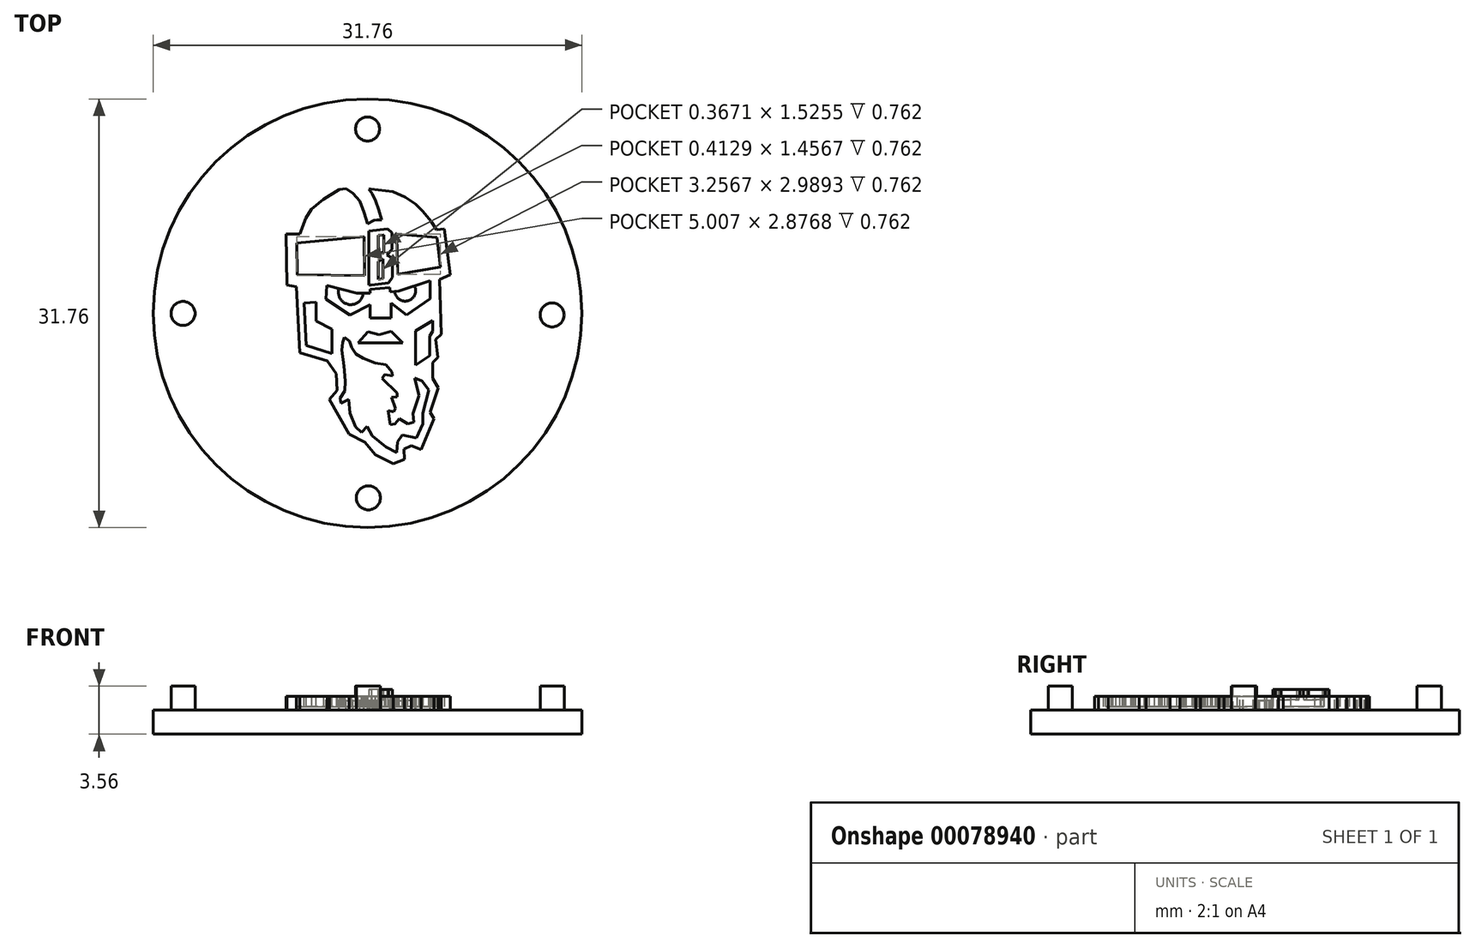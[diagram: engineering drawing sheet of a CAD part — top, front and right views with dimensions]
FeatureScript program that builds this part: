
annotation { "Feature Type Name" : "Feature", "Feature Type Description" : "" }
export const myFeature = defineFeature(function(context is Context, id is Id, definition is map)
    precondition{}
    {
        {
            var Q0;
            Q0=qCreatedBy(makeId("Top.planeOp"),FACE);
            var sketch = newSketch(context, id + "F0", { "sketchPlane" : qUnion([Q0])});
            skCircle(sketch, "E0", {"center": v(0, 0) * mm, "radius": 15.88 * mm});
            skSolve(sketch);
        }
        {
            var Q0;
            Q0=qSketchRegion(id+"F0",true);
            extrude(context, id + "F1", {"entities" : qUnion([Q0]), "oppositeDirection" : true, "depth" : 1.78 * mm});
        }
        {
            var Q0;
            Q0=makeQuery(id+"F1.opExtrude","CAP_FACE",FACE,{"disambiguationData":[OSD([sQuery(id+"F0.wireOp",EDGE,"E0")])],"isStart":true});
            var sketch = newSketch(context, id + "F2", { "sketchPlane" : qUnion([Q0])});
            skCircle(sketch, "E1", {"center": v(0, 0) * mm, "radius": 12.7 * mm});
            skSolve(sketch);
        }
        {
            var Q0;
            Q0=makeQuery(id+"F2.imprint","IMPRINT",FACE,{"disambiguationData":[TD([[makeQuery(id+"F2.imprint","IMPRINT",EDGE,{"derivedFrom":sQuery(id+"F2.wireOp",EDGE,"E1")}),-1.0]])]});
            var sketch = newSketch(context, id + "F3", { "sketchPlane" : qUnion([Q0])});
            skCircle(sketch, "E2", {"center": v(0, 13.65) * mm, "radius": 0.89 * mm});
            skCircle(sketch, "E3", {"center": v(-13.66, -0.02) * mm, "radius": 0.89 * mm});
            skCircle(sketch, "E4", {"center": v(0.06, -13.68) * mm, "radius": 0.89 * mm});
            skCircle(sketch, "E5", {"center": v(13.67, -0.12) * mm, "radius": 0.89 * mm});
            skSolve(sketch);
        }
        {
            var Q0;
            Q0=qSketchRegion(id+"F3",true);
            extrude(context, id + "F4", {"entities" : qUnion([Q0]), "operationType" : NewBodyOperationType.ADD, "depth" : 1.78 * mm});
        }
        {
            var Q0;
            Q0=makeQuery(id+"F2.imprint","IMPRINT",FACE,{"disambiguationData":[TD([[makeQuery(id+"F2.imprint","IMPRINT",EDGE,{"derivedFrom":sQuery(id+"F2.wireOp",EDGE,"E1")}),-1.0]])]});
            var sketch = newSketch(context, id + "F5", { "sketchPlane" : qUnion([Q0])});
            skLineSegment(sketch, "E6", {"start": v(-5.97, 2.09) * mm, "end": v(-6.04, 5.87) * mm});
            skLineSegment(sketch, "E7", {"start": v(-6.04, 5.87) * mm, "end": v(-5.01, 5.87) * mm});
            skLineSegment(sketch, "E8", {"start": v(-5.01, 5.87) * mm, "end": v(-4.57, 7.04) * mm});
            skLineSegment(sketch, "E9", {"start": v(-4.57, 7.04) * mm, "end": v(-4.15, 7.72) * mm});
            skLineSegment(sketch, "E10", {"start": v(-4.15, 7.72) * mm, "end": v(-3.26, 8.45) * mm});
            skLineSegment(sketch, "E11", {"start": v(-3.26, 8.45) * mm, "end": v(-2.1, 9.17) * mm});
            skLineSegment(sketch, "E12", {"start": v(-2.1, 9.17) * mm, "end": v(-1.1, 9.3) * mm});
            skLineSegment(sketch, "E13", {"start": v(-1.1, 9.3) * mm, "end": v(0.25, 9.2) * mm});
            skLineSegment(sketch, "E14", {"start": v(0.25, 9.2) * mm, "end": v(1.86, 9) * mm});
            skLineSegment(sketch, "E15", {"start": v(1.86, 9) * mm, "end": v(2.79, 8.58) * mm});
            skLineSegment(sketch, "E16", {"start": v(2.79, 8.58) * mm, "end": v(3.55, 8.1) * mm});
            skLineSegment(sketch, "E17", {"start": v(3.55, 8.1) * mm, "end": v(4.1, 7.55) * mm});
            skLineSegment(sketch, "E18", {"start": v(4.1, 7.55) * mm, "end": v(4.71, 6.83) * mm});
            skLineSegment(sketch, "E19", {"start": v(4.71, 6.83) * mm, "end": v(5.13, 6.18) * mm});
            skLineSegment(sketch, "E20", {"start": v(5.13, 6.18) * mm, "end": v(5.68, 6.25) * mm});
            skLineSegment(sketch, "E21", {"start": v(5.68, 6.25) * mm, "end": v(6.12, 2.84) * mm});
            skLineSegment(sketch, "E22", {"start": v(6.12, 2.84) * mm, "end": v(5.33, 2.5) * mm});
            skLineSegment(sketch, "E23", {"start": v(5.47, -1.56) * mm, "end": v(5.06, -1.93) * mm});
            skLineSegment(sketch, "E24", {"start": v(5.06, -1.93) * mm, "end": v(5.2, -3.27) * mm});
            skLineSegment(sketch, "E25", {"start": v(5.2, -3.27) * mm, "end": v(4.82, -3.65) * mm});
            skLineSegment(sketch, "E26", {"start": v(4.82, -3.65) * mm, "end": v(4.82, -4.82) * mm});
            skLineSegment(sketch, "E27", {"start": v(4.82, -4.82) * mm, "end": v(5.23, -5.54) * mm});
            skLineSegment(sketch, "E28", {"start": v(5.23, -5.54) * mm, "end": v(4.65, -7.33) * mm});
            skLineSegment(sketch, "E29", {"start": v(4.65, -7.33) * mm, "end": v(4.92, -7.81) * mm});
            skLineSegment(sketch, "E30", {"start": v(4.92, -7.81) * mm, "end": v(3.96, -10.11) * mm});
            skLineSegment(sketch, "E31", {"start": v(3.96, -10.11) * mm, "end": v(3.24, -9.8) * mm});
            skLineSegment(sketch, "E32", {"start": v(3.24, -9.8) * mm, "end": v(2.69, -10.08) * mm});
            skLineSegment(sketch, "E33", {"start": v(2.69, -10.08) * mm, "end": v(2.72, -10.84) * mm});
            skLineSegment(sketch, "E34", {"start": v(2.72, -10.84) * mm, "end": v(1.9, -11.15) * mm});
            skLineSegment(sketch, "E35", {"start": v(1.9, -11.15) * mm, "end": v(0.59, -10.5) * mm});
            skLineSegment(sketch, "E36", {"start": v(0.59, -10.5) * mm, "end": v(-0.2, -9.56) * mm});
            skLineSegment(sketch, "E37", {"start": v(-0.2, -9.56) * mm, "end": v(-1.37, -8.95) * mm});
            skLineSegment(sketch, "E38", {"start": v(-1.37, -8.95) * mm, "end": v(-2.81, -6.4) * mm});
            skLineSegment(sketch, "E39", {"start": v(-2.81, -6.4) * mm, "end": v(-2.26, -5.71) * mm});
            skLineSegment(sketch, "E40", {"start": v(-2.26, -5.71) * mm, "end": v(-2.33, -4.48) * mm});
            skLineSegment(sketch, "E41", {"start": v(-2.33, -4.48) * mm, "end": v(-2.98, -3.52) * mm});
            skLineSegment(sketch, "E42", {"start": v(-2.98, -3.52) * mm, "end": v(-5.01, -2.93) * mm});
            skLineSegment(sketch, "E43", {"start": v(-5.25, 1.95) * mm, "end": v(-5.97, 2.09) * mm});
            skLineSegment(sketch, "E44", {"start": v(-5.25, 1.95) * mm, "end": v(-5.01, -2.93) * mm});
            skLineSegment(sketch, "E45", {"start": v(5.33, 2.5) * mm, "end": v(5.47, -1.56) * mm});
            skSolve(sketch);
        }
        {
            var Q0;
            Q0 = qSketchRegion(id + "F5", true);
            extrude(context, id + "F6", {"entities" : qUnion([Q0]), "operationType" : NewBodyOperationType.ADD, "depth" : 1.02 * mm});
        }
        {
            var Q0;
            Q0=makeQuery(id+"F6.opExtrude","CAP_FACE",FACE,{"disambiguationData":[OSD([sQuery(id+"F5.wireOp",EDGE,"E6"),sQuery(id+"F5.wireOp",EDGE,"E7"),sQuery(id+"F5.wireOp",EDGE,"E8"),sQuery(id+"F5.wireOp",EDGE,"E9"),sQuery(id+"F5.wireOp",EDGE,"E10"),sQuery(id+"F5.wireOp",EDGE,"E11"),sQuery(id+"F5.wireOp",EDGE,"E12"),sQuery(id+"F5.wireOp",EDGE,"E13"),sQuery(id+"F5.wireOp",EDGE,"E14"),sQuery(id+"F5.wireOp",EDGE,"E15"),sQuery(id+"F5.wireOp",EDGE,"E16"),sQuery(id+"F5.wireOp",EDGE,"E17"),sQuery(id+"F5.wireOp",EDGE,"E18"),sQuery(id+"F5.wireOp",EDGE,"E19"),sQuery(id+"F5.wireOp",EDGE,"E20"),sQuery(id+"F5.wireOp",EDGE,"E21"),sQuery(id+"F5.wireOp",EDGE,"E22"),sQuery(id+"F5.wireOp",EDGE,"E23"),sQuery(id+"F5.wireOp",EDGE,"E24"),sQuery(id+"F5.wireOp",EDGE,"E25"),sQuery(id+"F5.wireOp",EDGE,"E26"),sQuery(id+"F5.wireOp",EDGE,"E27"),sQuery(id+"F5.wireOp",EDGE,"E28"),sQuery(id+"F5.wireOp",EDGE,"E29"),sQuery(id+"F5.wireOp",EDGE,"E30"),sQuery(id+"F5.wireOp",EDGE,"E31"),sQuery(id+"F5.wireOp",EDGE,"E32"),sQuery(id+"F5.wireOp",EDGE,"E33"),sQuery(id+"F5.wireOp",EDGE,"E34"),sQuery(id+"F5.wireOp",EDGE,"E35"),sQuery(id+"F5.wireOp",EDGE,"E36"),sQuery(id+"F5.wireOp",EDGE,"E37"),sQuery(id+"F5.wireOp",EDGE,"E38"),sQuery(id+"F5.wireOp",EDGE,"E39"),sQuery(id+"F5.wireOp",EDGE,"E40"),sQuery(id+"F5.wireOp",EDGE,"E41"),sQuery(id+"F5.wireOp",EDGE,"E42"),sQuery(id+"F5.wireOp",EDGE,"E43"),sQuery(id+"F5.wireOp",EDGE,"E44"),sQuery(id+"F5.wireOp",EDGE,"E45")])],"isStart":false});
            var sketch = newSketch(context, id + "F7", { "sketchPlane" : qUnion([Q0])});
            skLineSegment(sketch, "E46", {"start": v(1.76, 2.54) * mm, "end": v(1.56, 2.25) * mm});
            skLineSegment(sketch, "E47", {"start": v(1.56, 2.25) * mm, "end": v(0.29, 2.1) * mm});
            skLineSegment(sketch, "E48", {"start": v(1.5, 6.25) * mm, "end": v(0.11, 6.1) * mm});
            skLineSegment(sketch, "E49", {"start": v(0.11, 6.1) * mm, "end": v(0.11, 2.08) * mm});
            skLineSegment(sketch, "E50", {"start": v(0.11, 2.08) * mm, "end": v(0.29, 2.1) * mm});
            skLineSegment(sketch, "E51", {"start": v(1.76, 2.54) * mm, "end": v(1.85, 2.68) * mm});
            skLineSegment(sketch, "E52", {"start": v(1.85, 2.68) * mm, "end": v(1.85, 4.08) * mm});
            skLineSegment(sketch, "E53", {"start": v(1.82, 4.72) * mm, "end": v(1.82, 5.96) * mm});
            skLineSegment(sketch, "E54", {"start": v(1.82, 5.96) * mm, "end": v(1.5, 6.25) * mm});
            skLineSegment(sketch, "E55", {"start": v(1.85, 4.08) * mm, "end": v(1.44, 4.32) * mm});
            skLineSegment(sketch, "E56", {"start": v(1.44, 4.32) * mm, "end": v(1.82, 4.72) * mm});
            skSolve(sketch);
        }
        {
            var Q0;
            Q0 = qSketchRegion(id + "F7", true);
            extrude(context, id + "F8", {"entities" : qUnion([Q0]), "operationType" : NewBodyOperationType.ADD, "depth" : 0.5 * mm});
        }
        {
            var Q0;
            Q0=makeQuery(id+"F8.opExtrude","CAP_FACE",FACE,{"disambiguationData":[OSD([sQuery(id+"F7.wireOp",EDGE,"fYX4uZuE-G3KO-kAFN-Q3tX-kjtKbBJFoakh"),sQuery(id+"F7.wireOp",EDGE,"YPmriUSY-hdAp-dQCe-8mBx-pWrRA5I0jtpz"),sQuery(id+"F7.wireOp",EDGE,"z7Qzhmuc-i2NW-aavj-4vSp-u2Y9M5CnwlP8"),sQuery(id+"F7.wireOp",EDGE,"ckSUy8qp-SA3c-FUe3-0Q31-KxK1UnF4vGYb"),sQuery(id+"F7.wireOp",EDGE,"sxyVmpqT-fyA1-mW33-j374-GcPe8uCOevbE"),sQuery(id+"F7.wireOp",EDGE,"K1yYejpL-Rl0o-4VMU-6FDC-4IuAW9tG96Hq"),sQuery(id+"F7.wireOp",EDGE,"E46"),sQuery(id+"F7.wireOp",EDGE,"E47"),sQuery(id+"F7.wireOp",EDGE,"CEOLPyhg-Qa5c-qZ7R-2YQ4-FfNo4KrpU84Y")])],"isStart":false});
            var sketch = newSketch(context, id + "F9", { "sketchPlane" : qUnion([Q0])});
            skLineSegment(sketch, "E57", {"start": v(0.78, 4.36) * mm, "end": v(1.2, 4.58) * mm});
            skLineSegment(sketch, "E58", {"start": v(1.2, 4.58) * mm, "end": v(1.2, 5.82) * mm});
            skLineSegment(sketch, "E59", {"start": v(1.2, 5.82) * mm, "end": v(0.8, 5.76) * mm});
            skLineSegment(sketch, "E60", {"start": v(0.8, 5.76) * mm, "end": v(0.78, 4.36) * mm});
            skLineSegment(sketch, "E61", {"start": v(0.8, 3.84) * mm, "end": v(0.8, 2.5) * mm});
            skLineSegment(sketch, "E62", {"start": v(0.8, 2.5) * mm, "end": v(1.16, 2.57) * mm});
            skLineSegment(sketch, "E63", {"start": v(1.16, 2.57) * mm, "end": v(1.16, 4.03) * mm});
            skLineSegment(sketch, "E64", {"start": v(1.16, 4.03) * mm, "end": v(0.8, 3.84) * mm});
            skSolve(sketch);
        }
        {
            var Q0;
            Q0 = qSketchRegion(id + "F9", true);
            extrude(context, id + "F10", {"entities" : qUnion([Q0]), "operationType" : NewBodyOperationType.REMOVE, "oppositeDirection" : true, "depth" : 0.76 * mm});
        }
        {
            var Q0;
            Q0=makeQuery(id+"F6.opExtrude","CAP_FACE",FACE,{"disambiguationData":[OSD([sQuery(id+"F5.wireOp",EDGE,"E6"),sQuery(id+"F5.wireOp",EDGE,"E7"),sQuery(id+"F5.wireOp",EDGE,"E8"),sQuery(id+"F5.wireOp",EDGE,"E9"),sQuery(id+"F5.wireOp",EDGE,"E10"),sQuery(id+"F5.wireOp",EDGE,"E11"),sQuery(id+"F5.wireOp",EDGE,"E12"),sQuery(id+"F5.wireOp",EDGE,"E13"),sQuery(id+"F5.wireOp",EDGE,"E14"),sQuery(id+"F5.wireOp",EDGE,"E15"),sQuery(id+"F5.wireOp",EDGE,"E16"),sQuery(id+"F5.wireOp",EDGE,"E17"),sQuery(id+"F5.wireOp",EDGE,"E18"),sQuery(id+"F5.wireOp",EDGE,"E19"),sQuery(id+"F5.wireOp",EDGE,"E20"),sQuery(id+"F5.wireOp",EDGE,"E21"),sQuery(id+"F5.wireOp",EDGE,"E22"),sQuery(id+"F5.wireOp",EDGE,"E23"),sQuery(id+"F5.wireOp",EDGE,"E24"),sQuery(id+"F5.wireOp",EDGE,"E25"),sQuery(id+"F5.wireOp",EDGE,"E26"),sQuery(id+"F5.wireOp",EDGE,"E27"),sQuery(id+"F5.wireOp",EDGE,"E28"),sQuery(id+"F5.wireOp",EDGE,"E29"),sQuery(id+"F5.wireOp",EDGE,"E30"),sQuery(id+"F5.wireOp",EDGE,"E31"),sQuery(id+"F5.wireOp",EDGE,"E32"),sQuery(id+"F5.wireOp",EDGE,"E33"),sQuery(id+"F5.wireOp",EDGE,"E34"),sQuery(id+"F5.wireOp",EDGE,"E35"),sQuery(id+"F5.wireOp",EDGE,"E36"),sQuery(id+"F5.wireOp",EDGE,"E37"),sQuery(id+"F5.wireOp",EDGE,"E38"),sQuery(id+"F5.wireOp",EDGE,"E39"),sQuery(id+"F5.wireOp",EDGE,"E40"),sQuery(id+"F5.wireOp",EDGE,"E41"),sQuery(id+"F5.wireOp",EDGE,"E42"),sQuery(id+"F5.wireOp",EDGE,"E43"),sQuery(id+"F5.wireOp",EDGE,"E44"),sQuery(id+"F5.wireOp",EDGE,"E45")])],"isStart":false});
            var sketch = newSketch(context, id + "F11", { "sketchPlane" : qUnion([Q0])});
            skLineSegment(sketch, "E65", {"start": v(-5.23, 5.2) * mm, "end": v(-5.2, 2.85) * mm});
            skLineSegment(sketch, "E66", {"start": v(-5.2, 2.85) * mm, "end": v(-0.22, 2.8) * mm});
            skLineSegment(sketch, "E67", {"start": v(-0.22, 2.8) * mm, "end": v(-0.24, 5.68) * mm});
            skLineSegment(sketch, "E68", {"start": v(-0.24, 5.68) * mm, "end": v(-5.23, 5.2) * mm});
            skLineSegment(sketch, "E69", {"start": v(2.15, 5.87) * mm, "end": v(5.14, 5.6) * mm});
            skLineSegment(sketch, "E70", {"start": v(5.14, 5.6) * mm, "end": v(5.41, 3.42) * mm});
            skLineSegment(sketch, "E71", {"start": v(5.41, 3.42) * mm, "end": v(2.23, 2.88) * mm});
            skLineSegment(sketch, "E72", {"start": v(2.23, 2.88) * mm, "end": v(2.15, 5.87) * mm});
            skSolve(sketch);
        }
        {
            var Q0;
            Q0 = qSketchRegion(id + "F11", true);
            extrude(context, id + "F12", {"entities" : qUnion([Q0]), "operationType" : NewBodyOperationType.REMOVE, "oppositeDirection" : true, "depth" : 0.76 * mm});
        }
        {
            var Q0;
            Q0=makeQuery(id+"F6.opExtrude","CAP_FACE",FACE,{"disambiguationData":[OSD([sQuery(id+"F5.wireOp",EDGE,"E6"),sQuery(id+"F5.wireOp",EDGE,"E7"),sQuery(id+"F5.wireOp",EDGE,"E8"),sQuery(id+"F5.wireOp",EDGE,"E9"),sQuery(id+"F5.wireOp",EDGE,"E10"),sQuery(id+"F5.wireOp",EDGE,"E11"),sQuery(id+"F5.wireOp",EDGE,"E12"),sQuery(id+"F5.wireOp",EDGE,"E13"),sQuery(id+"F5.wireOp",EDGE,"E14"),sQuery(id+"F5.wireOp",EDGE,"E15"),sQuery(id+"F5.wireOp",EDGE,"E16"),sQuery(id+"F5.wireOp",EDGE,"E17"),sQuery(id+"F5.wireOp",EDGE,"E18"),sQuery(id+"F5.wireOp",EDGE,"E19"),sQuery(id+"F5.wireOp",EDGE,"E20"),sQuery(id+"F5.wireOp",EDGE,"E21"),sQuery(id+"F5.wireOp",EDGE,"E22"),sQuery(id+"F5.wireOp",EDGE,"E23"),sQuery(id+"F5.wireOp",EDGE,"E24"),sQuery(id+"F5.wireOp",EDGE,"E25"),sQuery(id+"F5.wireOp",EDGE,"E26"),sQuery(id+"F5.wireOp",EDGE,"E27"),sQuery(id+"F5.wireOp",EDGE,"E28"),sQuery(id+"F5.wireOp",EDGE,"E29"),sQuery(id+"F5.wireOp",EDGE,"E30"),sQuery(id+"F5.wireOp",EDGE,"E31"),sQuery(id+"F5.wireOp",EDGE,"E32"),sQuery(id+"F5.wireOp",EDGE,"E33"),sQuery(id+"F5.wireOp",EDGE,"E34"),sQuery(id+"F5.wireOp",EDGE,"E35"),sQuery(id+"F5.wireOp",EDGE,"E36"),sQuery(id+"F5.wireOp",EDGE,"E37"),sQuery(id+"F5.wireOp",EDGE,"E38"),sQuery(id+"F5.wireOp",EDGE,"E39"),sQuery(id+"F5.wireOp",EDGE,"E40"),sQuery(id+"F5.wireOp",EDGE,"E41"),sQuery(id+"F5.wireOp",EDGE,"E42"),sQuery(id+"F5.wireOp",EDGE,"E43"),sQuery(id+"F5.wireOp",EDGE,"E44"),sQuery(id+"F5.wireOp",EDGE,"E45")])],"isStart":false});
            var sketch = newSketch(context, id + "F13", { "sketchPlane" : qUnion([Q0])});
            skLineSegment(sketch, "E73", {"start": v(-3.03, 2.07) * mm, "end": v(-0.78, 1.48) * mm});
            skLineSegment(sketch, "E74", {"start": v(-0.78, 1.48) * mm, "end": v(0.2, 1.48) * mm});
            skLineSegment(sketch, "E75", {"start": v(0.2, 1.48) * mm, "end": v(0.2, 1.78) * mm});
            skLineSegment(sketch, "E76", {"start": v(0.2, 1.78) * mm, "end": v(1.65, 1.9) * mm});
            skLineSegment(sketch, "E77", {"start": v(1.65, 1.9) * mm, "end": v(1.68, 1.58) * mm});
            skLineSegment(sketch, "E78", {"start": v(1.68, 1.58) * mm, "end": v(2.32, 1.63) * mm});
            skLineSegment(sketch, "E79", {"start": v(2.32, 1.63) * mm, "end": v(4.64, 2.4) * mm});
            skLineSegment(sketch, "E80", {"start": v(4.64, 2.4) * mm, "end": v(4.64, 1.09) * mm});
            skLineSegment(sketch, "E81", {"start": v(4.64, 1.09) * mm, "end": v(2.89, -0.13) * mm});
            skLineSegment(sketch, "E82", {"start": v(2.89, -0.13) * mm, "end": v(1.73, 0.74) * mm});
            skLineSegment(sketch, "E83", {"start": v(1.73, 0.74) * mm, "end": v(1.73, -0.36) * mm});
            skLineSegment(sketch, "E84", {"start": v(1.73, -0.36) * mm, "end": v(0.18, -0.36) * mm});
            skLineSegment(sketch, "E85", {"start": v(0.18, -0.36) * mm, "end": v(0.18, 0.62) * mm});
            skLineSegment(sketch, "E86", {"start": v(0.18, 0.62) * mm, "end": v(-1.3, -0.14) * mm});
            skLineSegment(sketch, "E87", {"start": v(-1.3, -0.14) * mm, "end": v(-3.08, 1.04) * mm});
            skLineSegment(sketch, "E88", {"start": v(-3.08, 1.04) * mm, "end": v(-3.03, 2.07) * mm});
            skSolve(sketch);
        }
        {
            var Q0;
            Q0 = qSketchRegion(id + "F13", true);
            extrude(context, id + "F14", {"entities" : qUnion([Q0]), "operationType" : NewBodyOperationType.REMOVE, "oppositeDirection" : true, "depth" : 1.02 * mm});
        }
        {
            var Q0;
            Q0=makeQuery(id+"F2.imprint","IMPRINT",FACE,{"disambiguationData":[TD([[makeQuery(id+"F2.imprint","IMPRINT",EDGE,{"derivedFrom":sQuery(id+"F2.wireOp",EDGE,"E1")}),1.0]])]});
            var sketch = newSketch(context, id + "F15", { "sketchPlane" : qUnion([Q0])});
            skLineSegment(sketch, "E89", {"start": v(-2.11, 1.83) * mm, "end": v(-0.78, 1.48) * mm});
            skLineSegment(sketch, "E90", {"start": v(-0.78, 1.48) * mm, "end": v(-0.32, 1.48) * mm});
            skArc(sketch, "E91", {"start": v(-2.11, 1.83) * mm, "mid": v(-1.41, 0.65) * mm, "end": v(-0.32, 1.48) * mm});
            skLineSegment(sketch, "E92", {"start": v(3.48, 2.02) * mm, "end": v(2.32, 1.63) * mm});
            skLineSegment(sketch, "E93", {"start": v(2.32, 1.63) * mm, "end": v(2.02, 1.6) * mm});
            skArc(sketch, "E94", {"start": v(2.02, 1.6) * mm, "mid": v(3, 0.92) * mm, "end": v(3.48, 2.02) * mm});
            skSolve(sketch);
        }
        {
            var Q0;
            Q0 = qSketchRegion(id + "F15", true);
            extrude(context, id + "F16", {"entities" : qUnion([Q0]), "operationType" : NewBodyOperationType.ADD, "depth" : 0.71 * mm});
        }
        {
            var Q0;
            Q0=makeQuery(id+"F6.opExtrude","CAP_FACE",FACE,{"disambiguationData":[OSD([sQuery(id+"F5.wireOp",EDGE,"E6"),sQuery(id+"F5.wireOp",EDGE,"E7"),sQuery(id+"F5.wireOp",EDGE,"E8"),sQuery(id+"F5.wireOp",EDGE,"E9"),sQuery(id+"F5.wireOp",EDGE,"E10"),sQuery(id+"F5.wireOp",EDGE,"E11"),sQuery(id+"F5.wireOp",EDGE,"E12"),sQuery(id+"F5.wireOp",EDGE,"E13"),sQuery(id+"F5.wireOp",EDGE,"E14"),sQuery(id+"F5.wireOp",EDGE,"E15"),sQuery(id+"F5.wireOp",EDGE,"E16"),sQuery(id+"F5.wireOp",EDGE,"E17"),sQuery(id+"F5.wireOp",EDGE,"E18"),sQuery(id+"F5.wireOp",EDGE,"E19"),sQuery(id+"F5.wireOp",EDGE,"E20"),sQuery(id+"F5.wireOp",EDGE,"E21"),sQuery(id+"F5.wireOp",EDGE,"E22"),sQuery(id+"F5.wireOp",EDGE,"E23"),sQuery(id+"F5.wireOp",EDGE,"E24"),sQuery(id+"F5.wireOp",EDGE,"E25"),sQuery(id+"F5.wireOp",EDGE,"E26"),sQuery(id+"F5.wireOp",EDGE,"E27"),sQuery(id+"F5.wireOp",EDGE,"E28"),sQuery(id+"F5.wireOp",EDGE,"E29"),sQuery(id+"F5.wireOp",EDGE,"E30"),sQuery(id+"F5.wireOp",EDGE,"E31"),sQuery(id+"F5.wireOp",EDGE,"E32"),sQuery(id+"F5.wireOp",EDGE,"E33"),sQuery(id+"F5.wireOp",EDGE,"E34"),sQuery(id+"F5.wireOp",EDGE,"E35"),sQuery(id+"F5.wireOp",EDGE,"E36"),sQuery(id+"F5.wireOp",EDGE,"E37"),sQuery(id+"F5.wireOp",EDGE,"E38"),sQuery(id+"F5.wireOp",EDGE,"E39"),sQuery(id+"F5.wireOp",EDGE,"E40"),sQuery(id+"F5.wireOp",EDGE,"E41"),sQuery(id+"F5.wireOp",EDGE,"E42"),sQuery(id+"F5.wireOp",EDGE,"E43"),sQuery(id+"F5.wireOp",EDGE,"E44"),sQuery(id+"F5.wireOp",EDGE,"E45")])],"isStart":false});
            var sketch = newSketch(context, id + "F17", { "sketchPlane" : qUnion([Q0])});
            skLineSegment(sketch, "E95", {"start": v(-4.69, 0.77) * mm, "end": v(-4.53, -2.4) * mm});
            skLineSegment(sketch, "E96", {"start": v(-4.53, -2.4) * mm, "end": v(-2.62, -2.97) * mm});
            skLineSegment(sketch, "E97", {"start": v(-2.62, -2.97) * mm, "end": v(-2.62, -1.18) * mm});
            skLineSegment(sketch, "E98", {"start": v(-2.62, -1.18) * mm, "end": v(-3.81, -0.57) * mm});
            skLineSegment(sketch, "E99", {"start": v(-3.81, -0.57) * mm, "end": v(-3.81, 0.82) * mm});
            skLineSegment(sketch, "E100", {"start": v(-3.81, 0.82) * mm, "end": v(-4.69, 0.77) * mm});
            skLineSegment(sketch, "E101", {"start": v(4.84, -0.54) * mm, "end": v(4.84, -1.35) * mm});
            skLineSegment(sketch, "E102", {"start": v(4.84, -1.35) * mm, "end": v(4.6, -1.69) * mm});
            skLineSegment(sketch, "E103", {"start": v(4.6, -1.69) * mm, "end": v(4.6, -3.14) * mm});
            skLineSegment(sketch, "E104", {"start": v(4.6, -3.14) * mm, "end": v(3.57, -3.86) * mm});
            skLineSegment(sketch, "E105", {"start": v(3.57, -3.86) * mm, "end": v(3.57, -1.32) * mm});
            skLineSegment(sketch, "E106", {"start": v(3.57, -1.32) * mm, "end": v(4.84, -0.54) * mm});
            skSolve(sketch);
        }
        {
            var Q0;
            Q0 = qSketchRegion(id + "F17", true);
            extrude(context, id + "F18", {"entities" : qUnion([Q0]), "operationType" : NewBodyOperationType.REMOVE, "oppositeDirection" : true, "depth" : 0.76 * mm});
        }
        {
            var Q0;
            Q0=makeQuery(id+"F6.opExtrude","CAP_FACE",FACE,{"disambiguationData":[OSD([sQuery(id+"F5.wireOp",EDGE,"E6"),sQuery(id+"F5.wireOp",EDGE,"E7"),sQuery(id+"F5.wireOp",EDGE,"E8"),sQuery(id+"F5.wireOp",EDGE,"E9"),sQuery(id+"F5.wireOp",EDGE,"E10"),sQuery(id+"F5.wireOp",EDGE,"E11"),sQuery(id+"F5.wireOp",EDGE,"E12"),sQuery(id+"F5.wireOp",EDGE,"E13"),sQuery(id+"F5.wireOp",EDGE,"E14"),sQuery(id+"F5.wireOp",EDGE,"E15"),sQuery(id+"F5.wireOp",EDGE,"E16"),sQuery(id+"F5.wireOp",EDGE,"E17"),sQuery(id+"F5.wireOp",EDGE,"E18"),sQuery(id+"F5.wireOp",EDGE,"E19"),sQuery(id+"F5.wireOp",EDGE,"E20"),sQuery(id+"F5.wireOp",EDGE,"E21"),sQuery(id+"F5.wireOp",EDGE,"E22"),sQuery(id+"F5.wireOp",EDGE,"E23"),sQuery(id+"F5.wireOp",EDGE,"E24"),sQuery(id+"F5.wireOp",EDGE,"E25"),sQuery(id+"F5.wireOp",EDGE,"E26"),sQuery(id+"F5.wireOp",EDGE,"E27"),sQuery(id+"F5.wireOp",EDGE,"E28"),sQuery(id+"F5.wireOp",EDGE,"E29"),sQuery(id+"F5.wireOp",EDGE,"E30"),sQuery(id+"F5.wireOp",EDGE,"E31"),sQuery(id+"F5.wireOp",EDGE,"E32"),sQuery(id+"F5.wireOp",EDGE,"E33"),sQuery(id+"F5.wireOp",EDGE,"E34"),sQuery(id+"F5.wireOp",EDGE,"E35"),sQuery(id+"F5.wireOp",EDGE,"E36"),sQuery(id+"F5.wireOp",EDGE,"E37"),sQuery(id+"F5.wireOp",EDGE,"E38"),sQuery(id+"F5.wireOp",EDGE,"E39"),sQuery(id+"F5.wireOp",EDGE,"E40"),sQuery(id+"F5.wireOp",EDGE,"E41"),sQuery(id+"F5.wireOp",EDGE,"E42"),sQuery(id+"F5.wireOp",EDGE,"E43"),sQuery(id+"F5.wireOp",EDGE,"E44"),sQuery(id+"F5.wireOp",EDGE,"E45")])],"isStart":false});
            var sketch = newSketch(context, id + "F19", { "sketchPlane" : qUnion([Q0])});
            skLineSegment(sketch, "E107", {"start": v(4.04, -5.02) * mm, "end": v(4.54, -5.68) * mm});
            skLineSegment(sketch, "E108", {"start": v(4.54, -5.68) * mm, "end": v(4.1, -7.4) * mm});
            skLineSegment(sketch, "E109", {"start": v(4.1, -7.4) * mm, "end": v(4.11, -8.2) * mm});
            skLineSegment(sketch, "E110", {"start": v(4.11, -8.2) * mm, "end": v(3.61, -9.25) * mm});
            skLineSegment(sketch, "E111", {"start": v(3.61, -9.25) * mm, "end": v(2.57, -9.04) * mm});
            skLineSegment(sketch, "E112", {"start": v(2.57, -9.04) * mm, "end": v(2.22, -9.54) * mm});
            skLineSegment(sketch, "E113", {"start": v(2.22, -9.54) * mm, "end": v(2.15, -10.3) * mm});
            skLineSegment(sketch, "E114", {"start": v(2.15, -10.3) * mm, "end": v(1.35, -9.9) * mm});
            skLineSegment(sketch, "E115", {"start": v(1.35, -9.9) * mm, "end": v(0.35, -9.07) * mm});
            skLineSegment(sketch, "E116", {"start": v(0.35, -9.07) * mm, "end": v(-0.03, -8.4) * mm});
            skLineSegment(sketch, "E117", {"start": v(-0.03, -8.4) * mm, "end": v(-0.44, -8.82) * mm});
            skLineSegment(sketch, "E118", {"start": v(-0.44, -8.82) * mm, "end": v(-0.9, -8.42) * mm});
            skLineSegment(sketch, "E119", {"start": v(-0.9, -8.42) * mm, "end": v(-1.3, -7.42) * mm});
            skLineSegment(sketch, "E120", {"start": v(-1.3, -7.42) * mm, "end": v(-1.4, -6.37) * mm});
            skLineSegment(sketch, "E121", {"start": v(-1.4, -6.37) * mm, "end": v(-1.98, -6.68) * mm});
            skLineSegment(sketch, "E122", {"start": v(-1.98, -6.68) * mm, "end": v(-2.02, -6.3) * mm});
            skLineSegment(sketch, "E123", {"start": v(-2.02, -6.3) * mm, "end": v(-1.7, -5.74) * mm});
            skLineSegment(sketch, "E124", {"start": v(-1.7, -5.74) * mm, "end": v(-1.65, -5.02) * mm});
            skLineSegment(sketch, "E125", {"start": v(-1.65, -5.02) * mm, "end": v(-1.75, -3.9) * mm});
            skLineSegment(sketch, "E126", {"start": v(-1.75, -3.9) * mm, "end": v(-1.9, -2.75) * mm});
            skLineSegment(sketch, "E127", {"start": v(-1.9, -2.75) * mm, "end": v(-1.83, -2.15) * mm});
            skLineSegment(sketch, "E128", {"start": v(-0.32, -3.35) * mm, "end": v(0.56, -3.7) * mm});
            skLineSegment(sketch, "E129", {"start": v(0.56, -3.7) * mm, "end": v(1.37, -3.83) * mm});
            skLineSegment(sketch, "E130", {"start": v(1.37, -3.83) * mm, "end": v(1.82, -4.35) * mm});
            skLineSegment(sketch, "E131", {"start": v(1.82, -4.35) * mm, "end": v(1.84, -4.66) * mm});
            skLineSegment(sketch, "E132", {"start": v(1.84, -4.66) * mm, "end": v(1.26, -4.56) * mm});
            skLineSegment(sketch, "E133", {"start": v(1.26, -4.56) * mm, "end": v(1.08, -4.83) * mm});
            skLineSegment(sketch, "E134", {"start": v(1.08, -4.83) * mm, "end": v(2.18, -5.91) * mm});
            skLineSegment(sketch, "E135", {"start": v(2.18, -5.91) * mm, "end": v(2.2, -6.2) * mm});
            skLineSegment(sketch, "E136", {"start": v(2.2, -6.2) * mm, "end": v(1.78, -6.24) * mm});
            skLineSegment(sketch, "E137", {"start": v(1.78, -6.24) * mm, "end": v(2.07, -7.07) * mm});
            skLineSegment(sketch, "E138", {"start": v(2.07, -7.07) * mm, "end": v(1.95, -7.32) * mm});
            skLineSegment(sketch, "E139", {"start": v(1.95, -7.32) * mm, "end": v(1.53, -7.22) * mm});
            skLineSegment(sketch, "E140", {"start": v(1.53, -7.22) * mm, "end": v(1.68, -8.26) * mm});
            skLineSegment(sketch, "E141", {"start": v(1.68, -8.26) * mm, "end": v(2.03, -8.2) * mm});
            skLineSegment(sketch, "E142", {"start": v(2.03, -8.2) * mm, "end": v(2.36, -7.8) * mm});
            skLineSegment(sketch, "E143", {"start": v(3.44, -8.07) * mm, "end": v(3.38, -7.43) * mm});
            skLineSegment(sketch, "E144", {"start": v(3.38, -7.43) * mm, "end": v(3.82, -6.1) * mm});
            skLineSegment(sketch, "E145", {"start": v(3.82, -6.1) * mm, "end": v(3.5, -4.81) * mm});
            skLineSegment(sketch, "E146", {"start": v(3.5, -4.81) * mm, "end": v(4.04, -5.02) * mm});
            skLineSegment(sketch, "E147", {"start": v(-1.83, -2.15) * mm, "end": v(-1.7, -1.8) * mm});
            skLineSegment(sketch, "E148", {"start": v(-0.32, -3.35) * mm, "end": v(-0.84, -3.02) * mm});
            skLineSegment(sketch, "E149", {"start": v(-0.84, -3.02) * mm, "end": v(-1.17, -2.54) * mm});
            skLineSegment(sketch, "E150", {"start": v(-1.17, -2.54) * mm, "end": v(-1.33, -2.08) * mm});
            skLineSegment(sketch, "E151", {"start": v(-1.33, -2.08) * mm, "end": v(-1.7, -1.8) * mm});
            skLineSegment(sketch, "E152", {"start": v(3.44, -8.07) * mm, "end": v(3, -8.2) * mm});
            skLineSegment(sketch, "E153", {"start": v(3, -8.2) * mm, "end": v(2.36, -7.8) * mm});
            skSolve(sketch);
        }
        {
            var Q0;
            Q0 = qSketchRegion(id + "F19", true);
            extrude(context, id + "F20", {"entities" : qUnion([Q0]), "operationType" : NewBodyOperationType.REMOVE, "oppositeDirection" : true, "depth" : 0.76 * mm});
        }
        {
            var Q0;
            Q0=makeQuery(id+"F6.opExtrude","CAP_FACE",FACE,{"disambiguationData":[OSD([sQuery(id+"F5.wireOp",EDGE,"E6"),sQuery(id+"F5.wireOp",EDGE,"E7"),sQuery(id+"F5.wireOp",EDGE,"E8"),sQuery(id+"F5.wireOp",EDGE,"E9"),sQuery(id+"F5.wireOp",EDGE,"E10"),sQuery(id+"F5.wireOp",EDGE,"E11"),sQuery(id+"F5.wireOp",EDGE,"E12"),sQuery(id+"F5.wireOp",EDGE,"E13"),sQuery(id+"F5.wireOp",EDGE,"E14"),sQuery(id+"F5.wireOp",EDGE,"E15"),sQuery(id+"F5.wireOp",EDGE,"E16"),sQuery(id+"F5.wireOp",EDGE,"E17"),sQuery(id+"F5.wireOp",EDGE,"E18"),sQuery(id+"F5.wireOp",EDGE,"E19"),sQuery(id+"F5.wireOp",EDGE,"E20"),sQuery(id+"F5.wireOp",EDGE,"E21"),sQuery(id+"F5.wireOp",EDGE,"E22"),sQuery(id+"F5.wireOp",EDGE,"E23"),sQuery(id+"F5.wireOp",EDGE,"E24"),sQuery(id+"F5.wireOp",EDGE,"E25"),sQuery(id+"F5.wireOp",EDGE,"E26"),sQuery(id+"F5.wireOp",EDGE,"E27"),sQuery(id+"F5.wireOp",EDGE,"E28"),sQuery(id+"F5.wireOp",EDGE,"E29"),sQuery(id+"F5.wireOp",EDGE,"E30"),sQuery(id+"F5.wireOp",EDGE,"E31"),sQuery(id+"F5.wireOp",EDGE,"E32"),sQuery(id+"F5.wireOp",EDGE,"E33"),sQuery(id+"F5.wireOp",EDGE,"E34"),sQuery(id+"F5.wireOp",EDGE,"E35"),sQuery(id+"F5.wireOp",EDGE,"E36"),sQuery(id+"F5.wireOp",EDGE,"E37"),sQuery(id+"F5.wireOp",EDGE,"E38"),sQuery(id+"F5.wireOp",EDGE,"E39"),sQuery(id+"F5.wireOp",EDGE,"E40"),sQuery(id+"F5.wireOp",EDGE,"E41"),sQuery(id+"F5.wireOp",EDGE,"E42"),sQuery(id+"F5.wireOp",EDGE,"E43"),sQuery(id+"F5.wireOp",EDGE,"E44"),sQuery(id+"F5.wireOp",EDGE,"E45")])],"isStart":false});
            var sketch = newSketch(context, id + "F21", { "sketchPlane" : qUnion([Q0])});
            skLineSegment(sketch, "E154", {"start": v(-1.6, 9.24) * mm, "end": v(-1.1, 8.87) * mm});
            skLineSegment(sketch, "E155", {"start": v(-1.1, 8.87) * mm, "end": v(-0.57, 8.3) * mm});
            skLineSegment(sketch, "E156", {"start": v(-0.57, 8.3) * mm, "end": v(-0.25, 7.45) * mm});
            skLineSegment(sketch, "E157", {"start": v(-0.25, 7.45) * mm, "end": v(0, 6.64) * mm});
            skLineSegment(sketch, "E158", {"start": v(0, 6.64) * mm, "end": v(0.48, 6.9) * mm});
            skLineSegment(sketch, "E159", {"start": v(0.48, 6.9) * mm, "end": v(0.7, 6.93) * mm});
            skLineSegment(sketch, "E160", {"start": v(0.7, 6.93) * mm, "end": v(1.05, 6.91) * mm});
            skLineSegment(sketch, "E161", {"start": v(1.05, 6.91) * mm, "end": v(0.84, 7.67) * mm});
            skLineSegment(sketch, "E162", {"start": v(0.84, 7.67) * mm, "end": v(0.6, 8.32) * mm});
            skLineSegment(sketch, "E163", {"start": v(0.6, 8.32) * mm, "end": v(0.35, 8.84) * mm});
            skLineSegment(sketch, "E164", {"start": v(0.35, 8.84) * mm, "end": v(0.1, 9.21) * mm});
            skLineSegment(sketch, "E165", {"start": v(-1.6, 9.24) * mm, "end": v(-1.1, 9.3) * mm});
            skLineSegment(sketch, "E166", {"start": v(-1.1, 9.3) * mm, "end": v(0.1, 9.21) * mm});
            skSolve(sketch);
        }
        {
            var Q0;
            Q0 = qSketchRegion(id + "F21", true);
            extrude(context, id + "F22", {"entities" : qUnion([Q0]), "operationType" : NewBodyOperationType.REMOVE, "oppositeDirection" : true, "depth" : 1.02 * mm});
        }
        {
            var Q0;
            Q0=makeQuery(id+"F6.opExtrude","CAP_FACE",FACE,{"disambiguationData":[OSD([sQuery(id+"F5.wireOp",EDGE,"E6"),sQuery(id+"F5.wireOp",EDGE,"E7"),sQuery(id+"F5.wireOp",EDGE,"E8"),sQuery(id+"F5.wireOp",EDGE,"E9"),sQuery(id+"F5.wireOp",EDGE,"E10"),sQuery(id+"F5.wireOp",EDGE,"E11"),sQuery(id+"F5.wireOp",EDGE,"E12"),sQuery(id+"F5.wireOp",EDGE,"E13"),sQuery(id+"F5.wireOp",EDGE,"E14"),sQuery(id+"F5.wireOp",EDGE,"E15"),sQuery(id+"F5.wireOp",EDGE,"E16"),sQuery(id+"F5.wireOp",EDGE,"E17"),sQuery(id+"F5.wireOp",EDGE,"E18"),sQuery(id+"F5.wireOp",EDGE,"E19"),sQuery(id+"F5.wireOp",EDGE,"E20"),sQuery(id+"F5.wireOp",EDGE,"E21"),sQuery(id+"F5.wireOp",EDGE,"E22"),sQuery(id+"F5.wireOp",EDGE,"E23"),sQuery(id+"F5.wireOp",EDGE,"E24"),sQuery(id+"F5.wireOp",EDGE,"E25"),sQuery(id+"F5.wireOp",EDGE,"E26"),sQuery(id+"F5.wireOp",EDGE,"E27"),sQuery(id+"F5.wireOp",EDGE,"E28"),sQuery(id+"F5.wireOp",EDGE,"E29"),sQuery(id+"F5.wireOp",EDGE,"E30"),sQuery(id+"F5.wireOp",EDGE,"E31"),sQuery(id+"F5.wireOp",EDGE,"E32"),sQuery(id+"F5.wireOp",EDGE,"E33"),sQuery(id+"F5.wireOp",EDGE,"E34"),sQuery(id+"F5.wireOp",EDGE,"E35"),sQuery(id+"F5.wireOp",EDGE,"E36"),sQuery(id+"F5.wireOp",EDGE,"E37"),sQuery(id+"F5.wireOp",EDGE,"E38"),sQuery(id+"F5.wireOp",EDGE,"E39"),sQuery(id+"F5.wireOp",EDGE,"E40"),sQuery(id+"F5.wireOp",EDGE,"E41"),sQuery(id+"F5.wireOp",EDGE,"E42"),sQuery(id+"F5.wireOp",EDGE,"E43"),sQuery(id+"F5.wireOp",EDGE,"E44"),sQuery(id+"F5.wireOp",EDGE,"E45")])],"isStart":false});
            var sketch = newSketch(context, id + "F23", { "sketchPlane" : qUnion([Q0])});
            skLineSegment(sketch, "E167", {"start": v(0.05, -1.38) * mm, "end": v(0.87, -1.6) * mm});
            skLineSegment(sketch, "E168", {"start": v(0.87, -1.6) * mm, "end": v(1.76, -1.33) * mm});
            skLineSegment(sketch, "E169", {"start": v(1.76, -1.33) * mm, "end": v(2.6, -2.19) * mm});
            skLineSegment(sketch, "E170", {"start": v(2.6, -2.19) * mm, "end": v(-0.68, -2.19) * mm});
            skLineSegment(sketch, "E171", {"start": v(-0.68, -2.19) * mm, "end": v(0.05, -1.38) * mm});
            skSolve(sketch);
        }
        {
            var Q0;
            Q0 = qSketchRegion(id + "F23", true);
            extrude(context, id + "F24", {"entities" : qUnion([Q0]), "operationType" : NewBodyOperationType.REMOVE, "oppositeDirection" : true, "depth" : 0.76 * mm});
        }
    });
